# Revit family: HERZ Ball Valve With Lever Handle 2100
name_source: partatom
category: Rohrzubehör
revit_build: Autodesk Revit 2018 (Build: 20190510_1515(x64)
units: mm (PartAtom-declared; Revit-internal decimal feet)

## family parameters
Arbeitsebenenbasiert = Nein
Beim Laden mit Abzugskörper schneiden = Nein
Bemaßung runder Anschluss = Durchmesser verwenden
Gemeinsam genutzt = Nein
Immer vertikal = Ja
OmniClass-Nummer = 23.65.55.14
OmniClass-Titel = Valves for Liquid Services
Teiletyp = Unterbricht

## types (1)
- HERZ Ball Valve With Lever Handle 2100
    Application = For use in potable water istallations.
For use where one expects durability even if the working conditions.
We recommend the valve used in the fully open or closed position, not in mid positions.
Operate the valve at least twice per year.
    Ball = pressed brass, full bore, machined to a microsmooth finish, chrome platted
    Ball seals = PTFE
    Body = pressed DZR brass acc. EN 12420 (corrosive resistant)
    Handle = Aluminium alloy, green dipped
    Hersteller = HERZ Armaturen Ges.m.b.H
    Internal thread = acc. ISO7-1
    Max. operating pressure = 2500000.0 Pa
    Max. operating temperature = 85 °C
    Medium = Water
    Note = Pursuant to Article 33 of the REACH Regulation (EC No. 1907/2006), we are obliged to point out that the material lead is listed on the SVHC list and that all brass components manufactured in our products exceed 0.1% (w / w) lead (CAS: 7439-92-1 / EINECS: 231-100-4).
Since lead is a component part of an alloy, actual exposure is not possible and therefore no additional information on safe use is necessary.
    SCTWCODE = 04;04:02
    SCTWSEQ = FW;SBT_TYP_FW="103";2
    Spindle seals = EPDM
    URL = www.herzvalves.com
    W01 = 135.00°
